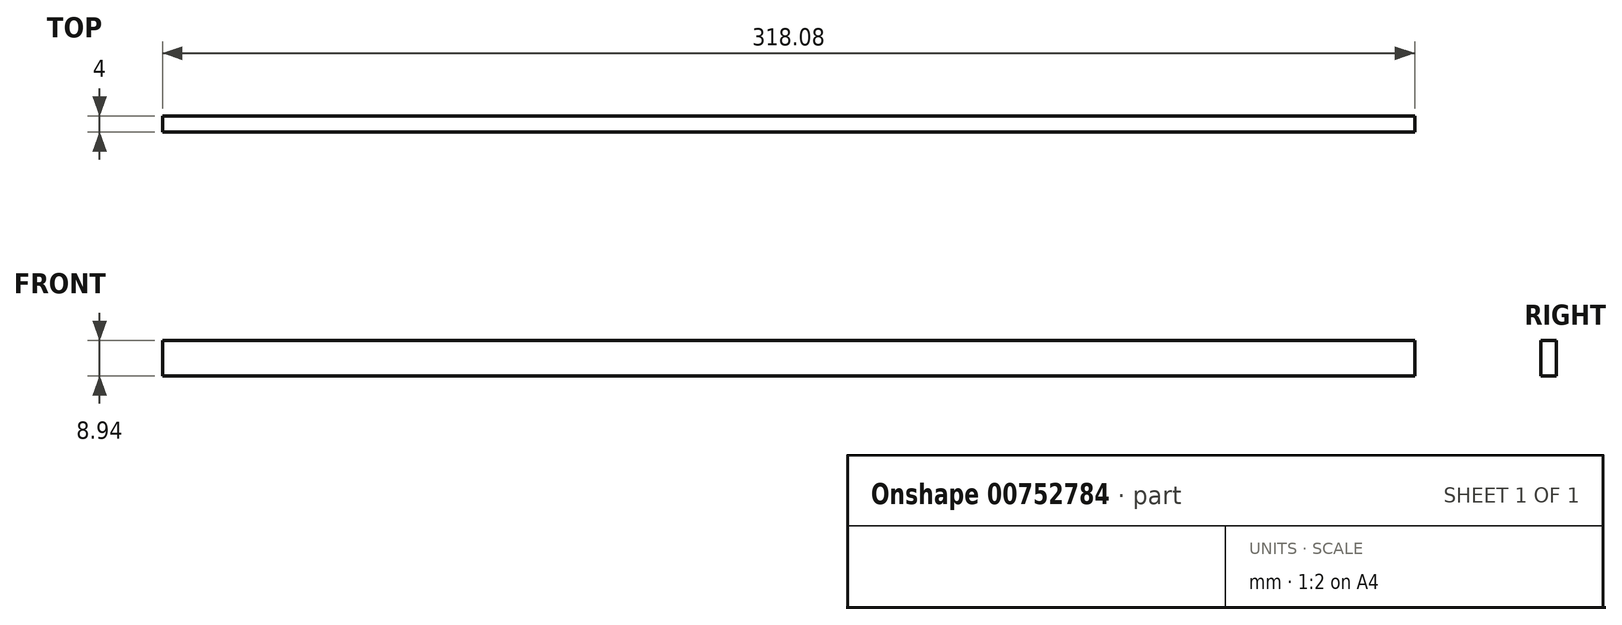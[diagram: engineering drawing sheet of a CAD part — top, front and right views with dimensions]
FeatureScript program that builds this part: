
annotation { "Feature Type Name" : "Feature", "Feature Type Description" : "" }
export const myFeature = defineFeature(function(context is Context, id is Id, definition is map)
    precondition{}
    {
        {
            var Q0;
            Q0=qCreatedBy(makeId("Front.planeOp"),FACE);
            var sketch = newSketch(context, id + "F0", { "sketchPlane" : qUnion([Q0])});
            skLineSegment(sketch, "E0.bottom", {"start": v(0, 0) * mm, "end": v(-318.08, 0) * mm});
            skLineSegment(sketch, "E0.top", {"start": v(0, 8.94) * mm, "end": v(-318.08, 8.94) * mm});
            skLineSegment(sketch, "E0.left", {"start": v(0, 0) * mm, "end": v(0, 8.94) * mm});
            skLineSegment(sketch, "E0.right", {"start": v(-318.08, 0) * mm, "end": v(-318.08, 8.94) * mm});
            skSolve(sketch);
        }
        {
            var Q0;
            Q0 = qSketchRegion(id + "F0", true);
            extrude(context, id + "F1", {"entities" : qUnion([Q0]), "depth" : 4 * mm, "offsetDistance" : 25 * mm});
        }
    });
